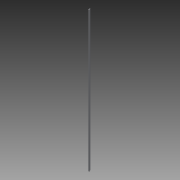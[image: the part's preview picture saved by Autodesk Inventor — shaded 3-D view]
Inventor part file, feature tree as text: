
AUTODESK INVENTOR PART (.ipt)
format: ipt  version: 2015 SP1 (Build 190203100, 203)  size: 76,288 bytes
history: native  units: mm
features: extrude x1, sketch x1
ambient origin geometry x8: Origin, YZ Plane, XZ Plane, XY Plane, X Axis, Y Axis, Z Axis, Center Point
bodies: Solid1 (feature_tree)
feature tree (2):
  extrude  "Extrusion1"  Depth=5.0mm
  sketch  "Sketch1"  dims[d1=30.0mm d2=5.0mm d3=20.0mm d4=5.0mm d5=5.0mm d6=2000.0mm d7=0.0mm]
